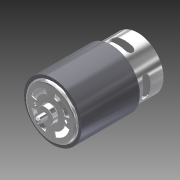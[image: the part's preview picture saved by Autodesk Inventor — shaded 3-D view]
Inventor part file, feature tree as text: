
AUTODESK INVENTOR PART (.ipt)
format: ipt  version: 2011 SP1 (Build 150282100, 282)  size: 346,112 bytes
history: native  units: mm (DEFAULTED — no unit token found)
features: sketch x15, extrude x13, fillet x3, pattern_circular x3, plane x3, hole x2, mirror x2, shell x1, chamfer x1
ambient origin geometry x8: Origin, YZ Plane, XZ Plane, XY Plane, X Axis, Y Axis, Z Axis, Center Point
bodies: Solid1 (feature_tree)
feature tree (43):
  extrude  "Extrusion1"  Depth=71.3mm TaperAngle=0.0deg
  fillet  "Fillet1"  Radius=2.0mm
  shell  "Shell1"  Thickness=0.62mm
  extrude  "Extrusion2"  Depth=4.5mm TaperAngle=0.0deg
  fillet  "Fillet2"  Radius=0.5mm
  extrude  "Extrusion3"  Depth=7.6mm TaperAngle=0.0deg
  fillet  "Fillet3"  Radius=2.5mm
  hole  "Hole1"  [1 undecoded]
  mirror  "Mirror1"
  extrude  "Extrusion4"  Depth=16.0mm
  pattern_circular  "Circular Pattern1"  Count=4 Angle=360.0deg
  plane  "Work Plane1"
  extrude  "Extrusion5"  Depth=0.62mm TaperAngle=0.0deg
  extrude  "Extrusion6"  Depth=0.62mm TaperAngle=0.0deg
  extrude  "Extrusion7"  Depth=3.0mm TaperAngle=0.0deg
  extrude  "Extrusion8"  Depth=0.8mm TaperAngle=0.0deg
  extrude  "Extrusion9"  Depth=1.0mm TaperAngle=0.0deg
  extrude  "Extrusion10"  Depth=3.15mm
  pattern_circular  "Circular Pattern2"  [2 undecoded]
  extrude  "Extrusion11"  Depth=1.0mm TaperAngle=0.0deg
  chamfer  "Chamfer1"  Distance=40.0mm Angle=360.0deg
  hole  "Hole2"  [1 undecoded]
  mirror  "Mirror2"
  plane  "Work Plane2"
  extrude  "Extrusion12"  Depth=3.8mm
  plane  "Work Plane3"
  extrude  "Flux Ring"  Depth=14.0mm
  pattern_circular  "Circular Pattern3"  [2 undecoded]
  sketch  "Sketch1"  dims[d0=42.1mm d1=71.3mm d2=0.0mm d3=2.0mm d4=0.62mm]
  sketch  "Sketch2"  dims[d5=13.0mm d6=4.5mm d7=0.0mm d8=0.5mm]
  sketch  "Sketch3"  dims[d9=5.0mm d10=7.6mm d11=0.0mm d12=2.5mm]
  sketch  "Sketch4"  dims[d13=12.5mm]
  sketch  "Sketch5"  dims[d14=2.5mm d15=6.0mm d16=4.0mm d17=2.0mm d18=14.3117mm d19=8.0mm d20=20.594885mm d21=15.0deg]
  sketch  "Sketch6"  dims[d22=15.0deg d23=16.0mm]
  sketch  "Sketch7"  dims[d24=12.0mm]
  sketch  "Sketch8"  dims[d25=10.0mm d26=0.0mm d27=40.0mm d29=360.0deg]
  sketch  "Sketch9"  dims[d30=-1.75mm d31=0.62mm d32=0.0mm]
  sketch  "Sketch10"  dims[d33=24.0mm d34=0.62mm d35=0.0mm]
  sketch  "Sketch11"  dims[d36=10.75mm d37=3.0mm d38=0.0mm]
  sketch  "Sketch12"  dims[d39=6.9mm d40=0.8mm d41=0.0mm]
  sketch  "Sketch13"  dims[d42=3.2mm d43=1.0mm d44=0.0mm]
  sketch  "Sketch14"  dims[d45=3.15mm d46=3.15mm]
  sketch  "Sketch15"  dims[d47=9.875mm d48=6.5mm d49=1.0mm d50=0.0mm d51=40.0mm d53=360.0deg d54=0.5mm d55=3.8mm d56=14.0mm d57=7.2mm d58=0.0mm d59=1.0mm d60=2.0mm d61=3.0mm d62=2.0mm d63=6.0mm d64=4.0mm d65=2.0mm d66=14.3117mm d67=1.0mm d68=20.594885mm d69=18.0mm d70=10.75mm d71=5.9mm d72=12.0mm d73=7.2mm d74=0.0mm d75=45.0deg d76=2.45mm d77=47.5mm d78=0.0mm d79=40.0mm d80=360.0deg]
note: 6 required parameter values undecoded (feature->parameter linkage not recoverable at this tier; creation-order binding heuristic only, values carry confidence <= 0.55)
